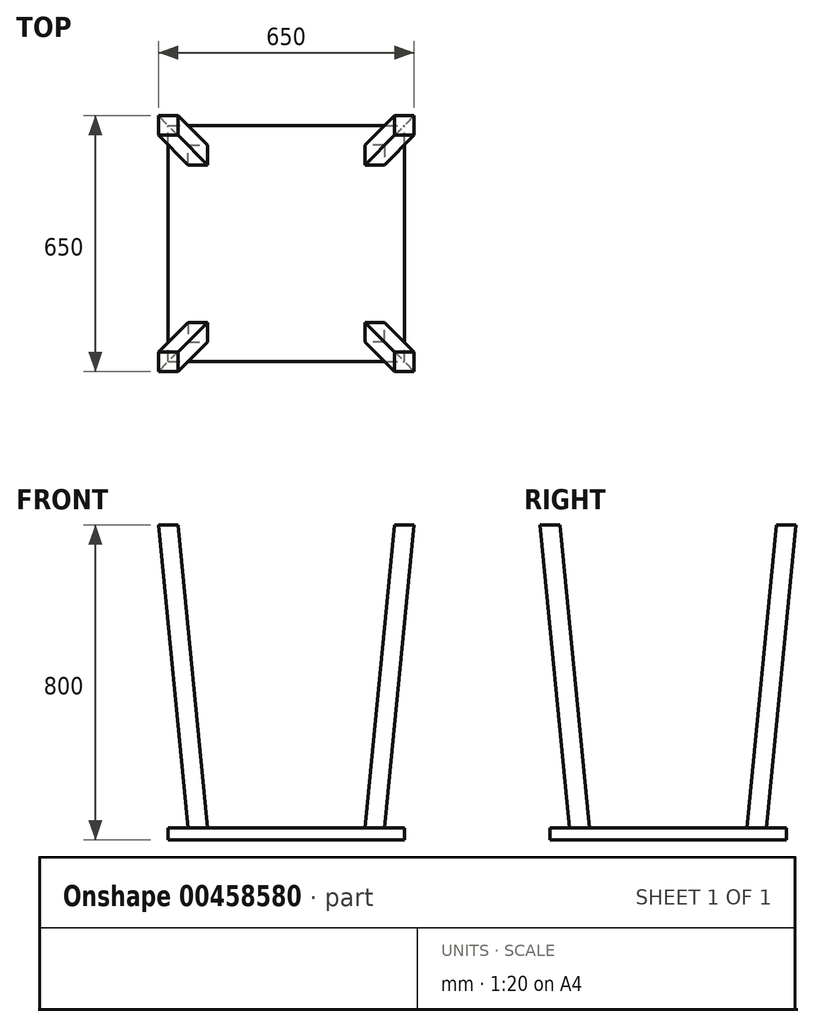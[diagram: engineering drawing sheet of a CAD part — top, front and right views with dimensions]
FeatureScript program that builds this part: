
annotation { "Feature Type Name" : "Feature", "Feature Type Description" : "" }
export const myFeature = defineFeature(function(context is Context, id is Id, definition is map)
    precondition{}
    {
        {
            var Q0;
            Q0=qCreatedBy(makeId("Top.planeOp"),FACE);
            var sketch = newSketch(context, id + "F0", { "sketchPlane" : qUnion([Q0])});
            skLineSegment(sketch, "E0.bottom", {"start": v(250, -250) * mm, "end": v(-250, -250) * mm});
            skLineSegment(sketch, "E0.top", {"start": v(250, 250) * mm, "end": v(-250, 250) * mm});
            skLineSegment(sketch, "E0.left", {"start": v(250, -250) * mm, "end": v(250, 250) * mm});
            skLineSegment(sketch, "E0.right", {"start": v(-250, -250) * mm, "end": v(-250, 250) * mm});
            skPoint(sketch, "E0.middle", {"position": v(0, 0) * mm});
            skLineSegment(sketch, "E1.bottom", {"start": v(-300, -300) * mm, "end": v(300, -300) * mm});
            skLineSegment(sketch, "E1.top", {"start": v(-300, 300) * mm, "end": v(300, 300) * mm});
            skLineSegment(sketch, "E1.left", {"start": v(-300, -300) * mm, "end": v(-300, 300) * mm});
            skLineSegment(sketch, "E1.right", {"start": v(300, -300) * mm, "end": v(300, 300) * mm});
            skSolve(sketch);
        }
        {
            var Q0;
            Q0=makeQuery(id+"F0.imprint","IMPRINT",FACE,{"disambiguationData":[TD([[makeQuery(id+"F0.imprint","IMPRINT",EDGE,{"derivedFrom":sQuery(id+"F0.wireOp",EDGE,"E0.bottom")}),-1.0]])]});
            var Q1;
            Q1=makeQuery(id+"F0.imprint","IMPRINT",FACE,{"disambiguationData":[TD([[makeQuery(id+"F0.imprint","IMPRINT",EDGE,{"derivedFrom":sQuery(id+"F0.wireOp",EDGE,"E0.bottom")}),1.0]])]});
            extrude(context, id + "F1", {"entities" : qUnion([Q0, Q1]), "depth" : 30 * mm});
        }
        {
            var Q0;
            Q0=makeQuery(id+"F1.opExtrude","CAP_FACE",FACE,{"disambiguationData":[OSD([sQuery(id+"F0.wireOp",EDGE,"E1.bottom"),sQuery(id+"F0.wireOp",EDGE,"E1.top"),sQuery(id+"F0.wireOp",EDGE,"E1.left"),sQuery(id+"F0.wireOp",EDGE,"E1.right")])],"isStart":false});
            var sketch = newSketch(context, id + "F2", { "sketchPlane" : qUnion([Q0])});
            skLineSegment(sketch, "E2.bottom", {"start": v(-250, -250) * mm, "end": v(250, -250) * mm});
            skLineSegment(sketch, "E2.top", {"start": v(-250, 250) * mm, "end": v(250, 250) * mm});
            skLineSegment(sketch, "E2.left", {"start": v(-250, -250) * mm, "end": v(-250, 250) * mm});
            skLineSegment(sketch, "E2.right", {"start": v(250, -250) * mm, "end": v(250, 250) * mm});
            skPoint(sketch, "E2.middle", {"position": v(0, 0) * mm});
            skLineSegment(sketch, "E3", {"start": v(-200, 250) * mm, "end": v(-200, 200) * mm});
            skLineSegment(sketch, "E4", {"start": v(-200, 200) * mm, "end": v(-250, 200) * mm});
            skSolve(sketch);
        }
        {
            var Q0;
            Q0=qCreatedBy(makeId("Top.planeOp"),FACE);
            cPlane(context, id + "F3", {"entities" : qUnion([Q0]), "cplaneType" : CPlaneType.OFFSET, "offset" : 800 * mm, "width" : 150 * mm, "height" : 150 * mm});
        }
        {
            var Q0;
            Q0=qCreatedBy(id+"F3.planeOp",FACE);
            var sketch = newSketch(context, id + "F4", { "sketchPlane" : qUnion([Q0])});
            skLineSegment(sketch, "E5.bottom", {"start": v(325, 325) * mm, "end": v(-325, 325) * mm});
            skLineSegment(sketch, "E5.top", {"start": v(325, -325) * mm, "end": v(-325, -325) * mm});
            skLineSegment(sketch, "E5.left", {"start": v(325, 325) * mm, "end": v(325, -325) * mm});
            skLineSegment(sketch, "E5.right", {"start": v(-325, 325) * mm, "end": v(-325, -325) * mm});
            skPoint(sketch, "E5.middle", {"position": v(0, 0) * mm});
            skLineSegment(sketch, "E6", {"start": v(-275, 325) * mm, "end": v(-275, 275) * mm});
            skLineSegment(sketch, "E7", {"start": v(-275, 275) * mm, "end": v(-325, 275) * mm});
            skSolve(sketch);
        }
        {
            var Q1;
            {var subQ3=sQuery(id+"F4.wireOp",EDGE,"E6");Q1=makeQuery(id+"F4.imprint","IMPRINT",FACE,{"disambiguationData":[TD([[makeQuery(id+"F4.imprint","IMPRINT",EDGE,{"derivedFrom":subQ3}),-1.0]])]});}
            var Q2;
            {var subQ3=sQuery(id+"F2.wireOp",EDGE,"E3");Q2=makeQuery(id+"F2.imprint","IMPRINT",FACE,{"disambiguationData":[TD([[makeQuery(id+"F2.imprint","IMPRINT",EDGE,{"derivedFrom":subQ3}),-1.0]])]});}
            loft(context, id + "F5", {"sheetProfilesArray" : [{ "sheetProfileEntities" : qUnion([Q1]) }, { "sheetProfileEntities" : qUnion([Q2]) }]});
        }
        {
            var Q0;
            Q0=makeQuery(id+"F1.opExtrude","CAP_FACE",FACE,{"disambiguationData":[OSD([sQuery(id+"F0.wireOp",EDGE,"E1.bottom"),sQuery(id+"F0.wireOp",EDGE,"E1.top"),sQuery(id+"F0.wireOp",EDGE,"E1.left"),sQuery(id+"F0.wireOp",EDGE,"E1.right")])],"isStart":false});
            var sketch = newSketch(context, id + "F6", { "sketchPlane" : qUnion([Q0])});
            skLineSegment(sketch, "E8.bottom", {"start": v(250, 250) * mm, "end": v(-250, 250) * mm});
            skLineSegment(sketch, "E8.top", {"start": v(250, -250) * mm, "end": v(-250, -250) * mm});
            skLineSegment(sketch, "E8.left", {"start": v(250, 250) * mm, "end": v(250, -250) * mm});
            skLineSegment(sketch, "E8.right", {"start": v(-250, 250) * mm, "end": v(-250, -250) * mm});
            skPoint(sketch, "E8.middle", {"position": v(0, 0) * mm});
            skLineSegment(sketch, "E9", {"start": v(200, 250) * mm, "end": v(200, 200) * mm});
            skLineSegment(sketch, "E10", {"start": v(200, 200) * mm, "end": v(250, 200) * mm});
            skSolve(sketch);
        }
        {
            var Q0;
            Q0=qCreatedBy(id+"F3.planeOp",FACE);
            var sketch = newSketch(context, id + "F7", { "sketchPlane" : qUnion([Q0])});
            skLineSegment(sketch, "E11.bottom", {"start": v(325, 325) * mm, "end": v(-325, 325) * mm});
            skLineSegment(sketch, "E11.top", {"start": v(325, -325) * mm, "end": v(-325, -325) * mm});
            skLineSegment(sketch, "E11.left", {"start": v(325, 325) * mm, "end": v(325, -325) * mm});
            skLineSegment(sketch, "E11.right", {"start": v(-325, 325) * mm, "end": v(-325, -325) * mm});
            skPoint(sketch, "E11.middle", {"position": v(0, 0) * mm});
            skLineSegment(sketch, "E12", {"start": v(275, 325) * mm, "end": v(275, 275) * mm});
            skLineSegment(sketch, "E13", {"start": v(275, 275) * mm, "end": v(325, 275) * mm});
            skSolve(sketch);
        }
        {
            var Q1;
            {var subQ3=sQuery(id+"F7.wireOp",EDGE,"E12");Q1=makeQuery(id+"F7.imprint","IMPRINT",FACE,{"disambiguationData":[TD([[makeQuery(id+"F7.imprint","IMPRINT",EDGE,{"derivedFrom":subQ3}),1.0]])]});}
            var Q2;
            {var subQ3=sQuery(id+"F6.wireOp",EDGE,"E9");Q2=makeQuery(id+"F6.imprint","IMPRINT",FACE,{"disambiguationData":[TD([[makeQuery(id+"F6.imprint","IMPRINT",EDGE,{"derivedFrom":subQ3}),1.0]])]});}
            loft(context, id + "F8", {"sheetProfilesArray" : [{ "sheetProfileEntities" : qUnion([Q1]) }, { "sheetProfileEntities" : qUnion([Q2]) }]});
        }
        {
            var Q0;
            {var subQ3=sQuery(id+"F4.wireOp",EDGE,"E6");var subQ8=sQuery(id+"F2.wireOp",EDGE,"E3");Q0=makeQuery(id+"F5.opLoft","SWEPT_BODY",BODY,{"disambiguationData":[OSD([makeQuery(id+"F2.imprint","IMPRINT",FACE,{"disambiguationData":[TD([[makeQuery(id+"F2.imprint","IMPRINT",EDGE,{"derivedFrom":subQ8}),-1.0]])]}),makeQuery(id+"F4.imprint","IMPRINT",FACE,{"disambiguationData":[TD([[makeQuery(id+"F4.imprint","IMPRINT",EDGE,{"derivedFrom":subQ3}),-1.0]])]})])]});}
            var Q1;
            {var subQ3=sQuery(id+"F7.wireOp",EDGE,"E12");var subQ8=sQuery(id+"F6.wireOp",EDGE,"E9");Q1=makeQuery(id+"F8.opLoft","SWEPT_BODY",BODY,{"disambiguationData":[OSD([makeQuery(id+"F6.imprint","IMPRINT",FACE,{"disambiguationData":[TD([[makeQuery(id+"F6.imprint","IMPRINT",EDGE,{"derivedFrom":subQ8}),1.0]])]}),makeQuery(id+"F7.imprint","IMPRINT",FACE,{"disambiguationData":[TD([[makeQuery(id+"F7.imprint","IMPRINT",EDGE,{"derivedFrom":subQ3}),1.0]])]})])]});}
            var Q2;
            Q2=qCreatedBy(makeId("Front.planeOp"),FACE);
            mirror(context, id + "F9", {"operationType" : NewBodyOperationType.ADD, "entities" : qUnion([Q0, Q1]), "mirrorPlane" : qUnion([Q2])});
        }
    });
